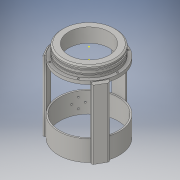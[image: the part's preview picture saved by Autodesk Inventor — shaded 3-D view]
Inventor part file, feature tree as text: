
AUTODESK INVENTOR PART (.ipt)
format: ipt  version: 2016 (Build 200138000, 138)  size: 306,688 bytes
history: native  units: in
note: dims shown in document units (in); Inventor stores cm internally (conversion verified against a paired STEP export)
features: sketch x16, extrude x13, plane x3, chamfer x2, fillet x1, revolve x1
ambient origin geometry x8: Origin, YZ Plane, XZ Plane, XY Plane, X Axis, Y Axis, Z Axis, Center Point
bodies: Solid1 (feature_tree)
feature tree (36):
  extrude  "Extrusion1"  Depth=0.3in TaperAngle=0.0deg
  extrude  "Extrusion2"  Depth=0.125in TaperAngle=0.0deg
  extrude  "Extrusion3"  Depth=3.875in
  sketch  "Sketch4"  dims[d9=0.125in d10=0.0in d11=4.0in]
  extrude  "Extrusion4"  Depth=4.0in
  extrude  "Extrusion5"  Depth=4.5in
  extrude  "Extrusion6"  Depth=0.1in TaperAngle=45.0deg
  chamfer  "Chamfer1"  Distance=2.3622in Angle=360.0deg
  extrude  "Extrusion7"  Depth=1.0in
  extrude  "Extrusion8"  Depth=5.0in TaperAngle=0.0deg
  extrude  "Extrusion9"  Depth=0.375in TaperAngle=0.0deg
  extrude  "Extrusion10"  Depth=0.375in TaperAngle=0.0deg
  extrude  "Extrusion11"  Depth=0.5in
  sketch  "Sketch13"  dims[d39=20.0in d40=0.0in d41=0.5in]
  extrude  "Extrusion12"  Depth=0.15in
  chamfer  "Chamfer2"  Distance=1.1811in Angle=360.0deg
  fillet  "Fillet1"  Radius=0.125in
  plane  "Work Plane1"
  revolve  "Revolution1"  [1 undecoded]
  plane  "Work Plane3"
  extrude  "Extrusion13"  Depth=1.527in
  sketch  "Sketch1"  dims[d0=4.0in d1=0.3in d2=0.0in]
  sketch  "Sketch2"  dims[d3=3.875in d4=0.125in d5=0.0in]
  sketch  "Sketch3"  dims[d6=0.3in d7=0.0in d8=3.875in]
  sketch  "Sketch5"  dims[d12=0.2in d13=0.0in d14=4.5in]
  sketch  "Sketch6"  dims[d15=0.24in d16=0.0in d17=0.1in d18=0.125in d19=45.0deg]
  sketch  "Sketch7"  dims[d20=0.138in]
  sketch  "Sketch8"  dims[d21=2.125in d22=2.3622in d24=360.0deg]
  sketch  "Sketch9"  dims[d26=0.24in d27=0.0in d28=1.0in]
  sketch  "Sketch10"  dims[d29=0.1in d31=5.0in d32=0.0in]
  sketch  "Sketch11"  dims[d33=3.0in d34=0.375in d35=0.0in]
  sketch  "Sketch12"  dims[d36=1.0in d37=0.375in d38=0.0in]
  sketch  "Sketch14"  dims[d42=0.5in d43=0.15in d44=1.1811in d46=360.0deg]
  sketch  "Sketch15"  dims[d48=5.0in d49=0.2in d50=0.0in d51=0.0in]
  plane  "Work Plane2"
  sketch  "Sketch16"  dims[d52=0.125in d53=0.125in d54=45.0deg d55=0.125in d58=0.1in d59=1.527in d60=90.0deg d61=-4.125in d64=0.118in d65=0.118in d66=0.118in d67=0.118in d68=0.74in d69=0.74in d70=0.74in d71=0.74in d72=5.0in d73=0.0in]
note: 1 required parameter value undecoded (feature->parameter linkage not recoverable at this tier; creation-order binding heuristic only, values carry confidence <= 0.55)
